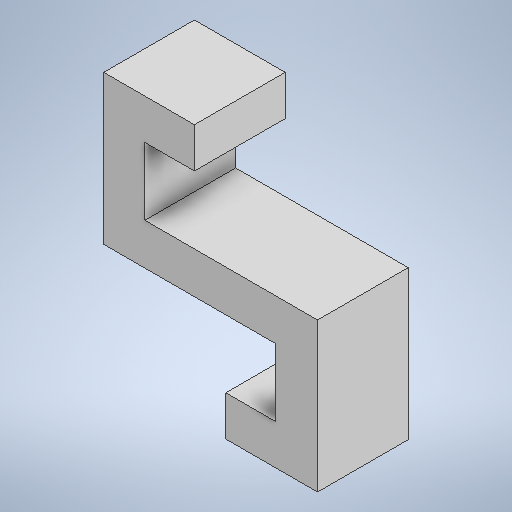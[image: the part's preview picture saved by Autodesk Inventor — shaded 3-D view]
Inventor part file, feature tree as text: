
AUTODESK INVENTOR PART (.ipt)
format: ipt  version: 2025 (Build 290162000, 162)  size: 236,032 bytes
history: native  units: mm
features: extrude x1, sketch x1
ambient origin geometry x8: Origin, YZ Plane, XZ Plane, XY Plane, X Axis, Y Axis, Z Axis, Center Point
bodies: Volumenkörper1 (feature_tree)
feature tree (2):
  extrude  "Extrusion1"  Depth=6.4mm
  sketch  "Skizze1"  dims[d10=8.6mm d11=0.0mm d12=6.4mm d13=3.8mm d14=6.4mm d15=3.925mm d16=3.9mm d17=3.8mm d18=4.7mm d19=4.7mm]
